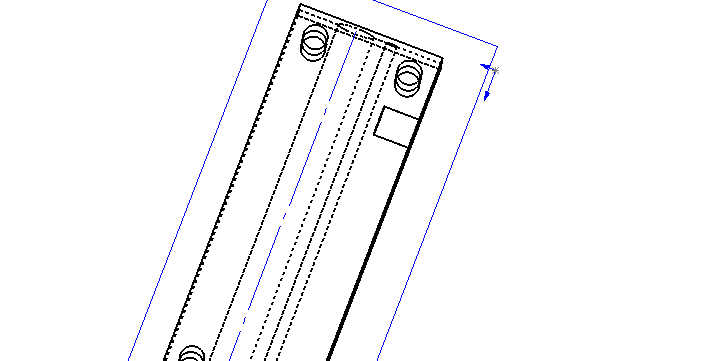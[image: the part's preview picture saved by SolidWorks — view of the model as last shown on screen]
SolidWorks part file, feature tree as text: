
SOLIDWORKS PART (.sldprt)
format: sldprt  version: not decoded by parser v0  size: 280,064 bytes
history: native  units: mm
features: sketch x5, cut_extrude x4, extrude x1, plane x1 (+11 scaffold rows collapsed)
feature tree (22):
  scaffold x11  (default folders/planes/origin — collapsed)
  sketch  "Sketch1"  dims[D1=66.675mm D2=25.4mm]
  extrude  "Extrude1"  Depth=12.7mm
  sketch  "Sketch2"  dims[D1=6.35mm D2=15.24mm D3=6.35mm]
  cut_extrude  "Cut-Extrude1"  [1 undecoded]
  sketch  "Sketch4"  dims[D1=5.08mm D2=12.7mm]
  cut_extrude  "Cut-Extrude3"  Depth=6.35mm
  sketch  "Sketch5"  dims[c1.D1=4.1148mm c1.D4=4.1275mm c1.D6=3.4925mm c1.D2=4.318mm c1.D3=4.318mm c1.D5=4.318mm c2.D6=33.3375mm]
  cut_extrude  "Cut-Extrude4"  [1 undecoded]
  sketch  "Sketch6"  dims[c1.D1=2.1082mm c1.D2=1.8796mm c2.D1=2.1082mm c2.D2=6.35mm c3.D1=6.35mm]
  cut_extrude  "Cut-Extrude6"  [1 undecoded]
  plane  "Plane1"  Offset=6.35mm
decode coverage: 7 of 10 modeling features carry decoded parameters
note: 3 parameter values undecoded
summary: no parameter record found for 3 features
note: suppression state not decoded; provenance and decode notes live in map.json
